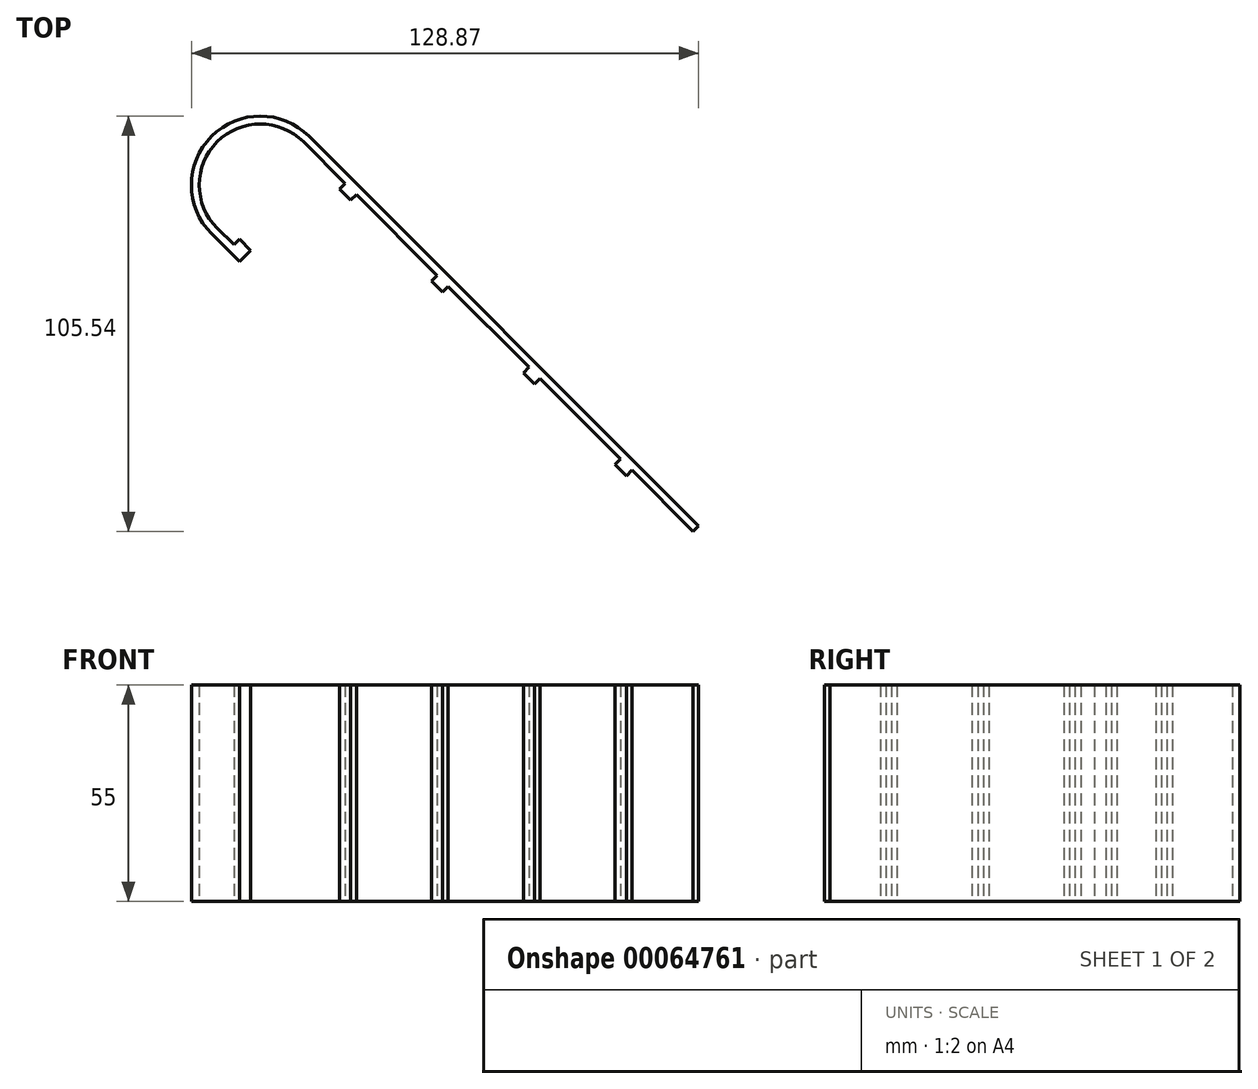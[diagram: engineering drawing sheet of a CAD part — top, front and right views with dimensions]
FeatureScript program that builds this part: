
annotation { "Feature Type Name" : "Feature", "Feature Type Description" : "" }
export const myFeature = defineFeature(function(context is Context, id is Id, definition is map)
    precondition{}
    {
        {
            var Q0;
            Q0=qCreatedBy(makeId("Top.planeOp"),FACE);
            var sketch = newSketch(context, id + "F0", { "sketchPlane" : qUnion([Q0])});
            skLineSegment(sketch, "E0", {"start": v(-75, 75) * mm, "end": v(-75, -75) * mm, "construction": true});
            skLineSegment(sketch, "E1", {"start": v(-75, -75) * mm, "end": v(75, -75) * mm, "construction": true});
            skLineSegment(sketch, "E2", {"start": v(75, -75) * mm, "end": v(75, 75) * mm, "construction": true});
            skLineSegment(sketch, "E3", {"start": v(75, 75) * mm, "end": v(-75, 75) * mm, "construction": true});
            skLineSegment(sketch, "E4", {"start": v(-75, 75) * mm, "end": v(75, -75) * mm, "construction": true});
            skLineSegment(sketch, "E5", {"start": v(64.65, -39.9) * mm, "end": v(-34.34, 59.1) * mm});
            skArc(sketch, "E6", {"start": v(-34.34, 59.1) * mm, "mid": v(-59.1, 59.1) * mm, "end": v(-59.1, 34.34) * mm});
            skLineSegment(sketch, "E7", {"start": v(-59.1, 34.34) * mm, "end": v(-34.34, 59.1) * mm, "construction": true});
            skLineSegment(sketch, "E8", {"start": v(-59.1, 34.34) * mm, "end": v(-52.02, 27.27) * mm});
            skLineSegment(sketch, "E9", {"start": v(-52.02, 27.27) * mm, "end": v(-50.6, 28.68) * mm});
            skLineSegment(sketch, "E10", {"start": v(-53.43, 31.51) * mm, "end": v(-57.68, 35.76) * mm});
            skLineSegment(sketch, "E11", {"start": v(64.65, -39.9) * mm, "end": v(63.24, -41.32) * mm});
            skLineSegment(sketch, "E12", {"start": v(63.24, -41.32) * mm, "end": v(47.68, -25.76) * mm});
            skArc(sketch, "E13", {"start": v(-57.68, 35.76) * mm, "mid": v(-57.68, 57.68) * mm, "end": v(-35.76, 57.68) * mm});
            skLineSegment(sketch, "E14", {"start": v(-25.15, 47.07) * mm, "end": v(-26.56, 45.66) * mm});
            skLineSegment(sketch, "E15", {"start": v(-26.56, 45.66) * mm, "end": v(-23.73, 42.83) * mm});
            skLineSegment(sketch, "E16", {"start": v(-23.73, 42.83) * mm, "end": v(-22.32, 44.24) * mm});
            skLineSegment(sketch, "E17.1.0.0", {"start": v(-1.81, 23.73) * mm, "end": v(-3.23, 22.32) * mm});
            skLineSegment(sketch, "E17.1.0.1", {"start": v(-3.23, 22.32) * mm, "end": v(-0.4, 19.5) * mm});
            skLineSegment(sketch, "E17.1.0.2", {"start": v(-0.4, 19.5) * mm, "end": v(1.01, 20.9) * mm});
            skLineSegment(sketch, "E17.2.0.0", {"start": v(21.52, 0.4) * mm, "end": v(20.1, -1.01) * mm});
            skLineSegment(sketch, "E17.2.0.1", {"start": v(20.1, -1.01) * mm, "end": v(22.93, -3.84) * mm});
            skLineSegment(sketch, "E17.2.0.2", {"start": v(22.93, -3.84) * mm, "end": v(24.35, -2.43) * mm});
            skLineSegment(sketch, "E17.3.0.0", {"start": v(44.85, -22.93) * mm, "end": v(43.44, -24.35) * mm});
            skLineSegment(sketch, "E17.3.0.1", {"start": v(43.44, -24.35) * mm, "end": v(46.27, -27.18) * mm});
            skLineSegment(sketch, "E17.3.0.2", {"start": v(46.27, -27.18) * mm, "end": v(47.68, -25.76) * mm});
            skLineSegment(sketch, "E17.direction1", {"start": v(-26.56, 45.66) * mm, "end": v(-3.23, 22.32) * mm, "construction": true});
            skLineSegment(sketch, "E18", {"start": v(-50.6, 28.68) * mm, "end": v(-49.2, 30.1) * mm});
            skLineSegment(sketch, "E19", {"start": v(-49.2, 30.1) * mm, "end": v(-52.02, 32.93) * mm});
            skLineSegment(sketch, "E20", {"start": v(-52.02, 32.93) * mm, "end": v(-53.43, 31.51) * mm});
            skLineSegment(sketch, "E21.trimOffspring", {"start": v(-25.15, 47.07) * mm, "end": v(-35.76, 57.68) * mm});
            skLineSegment(sketch, "E22.trimOffspring", {"start": v(-1.81, 23.73) * mm, "end": v(-22.32, 44.24) * mm});
            skLineSegment(sketch, "E23.trimOffspring", {"start": v(21.52, 0.4) * mm, "end": v(1.01, 20.9) * mm});
            skLineSegment(sketch, "E24.trimOffspring", {"start": v(44.85, -22.93) * mm, "end": v(24.35, -2.43) * mm});
            skSolve(sketch);
        }
        {
            var Q0;
            Q0 = qSketchRegion(id + "F0", true);
            extrude(context, id + "F1", {"entities" : qUnion([Q0]), "depth" : 55 * mm});
        }
    });
